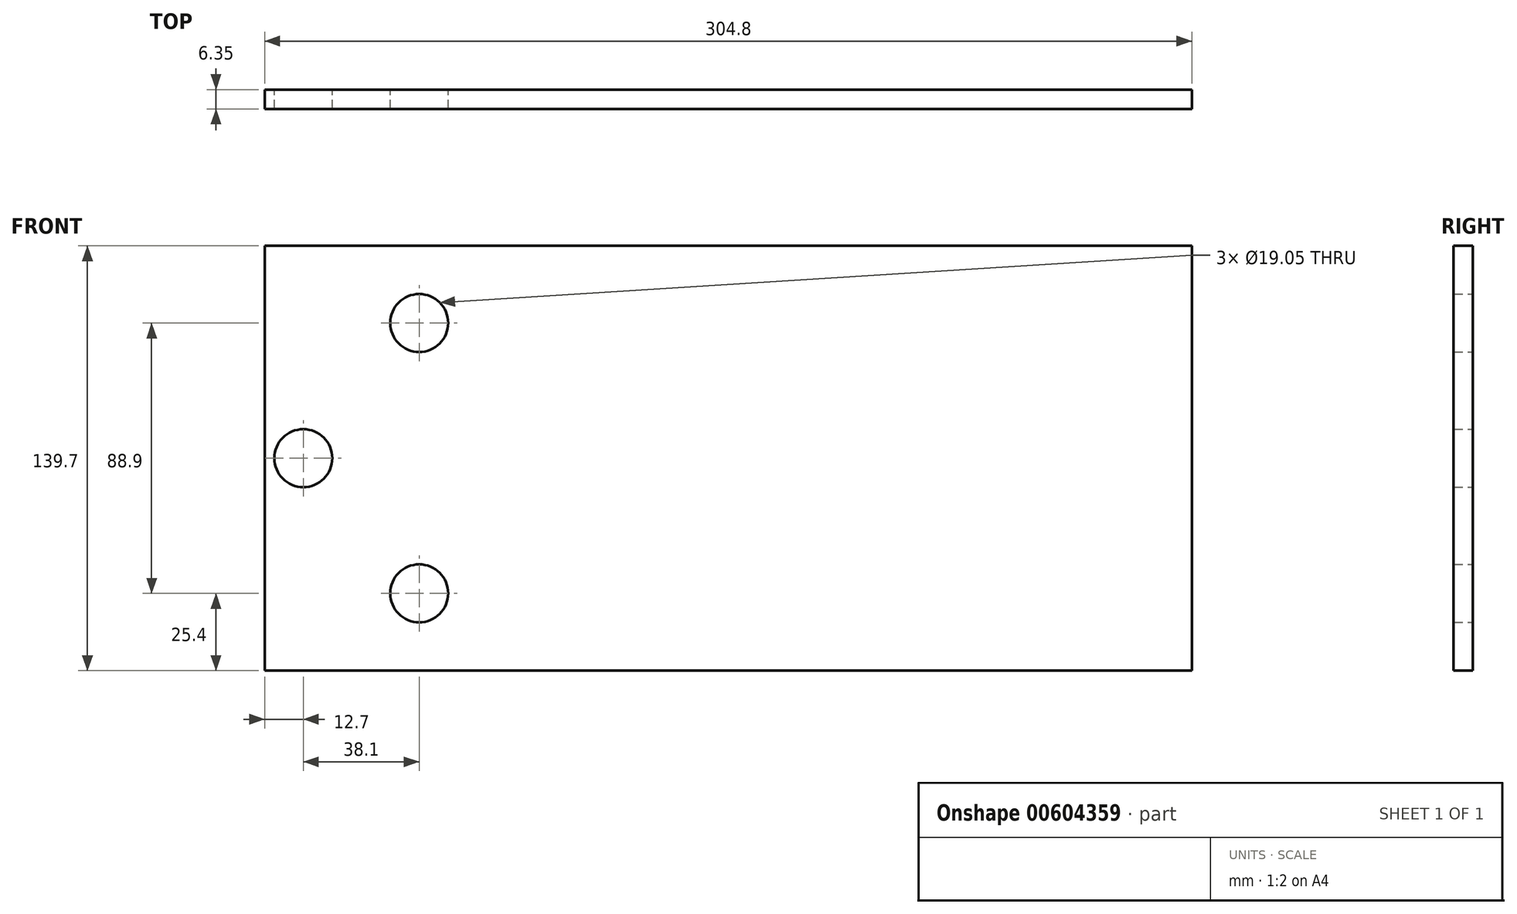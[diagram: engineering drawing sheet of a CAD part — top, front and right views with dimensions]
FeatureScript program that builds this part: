
annotation { "Feature Type Name" : "Feature", "Feature Type Description" : "" }
export const myFeature = defineFeature(function(context is Context, id is Id, definition is map)
    precondition{}
    {
        {
            var Q0;
            Q0=qCreatedBy(makeId("Front.planeOp"),FACE);
            var sketch = newSketch(context, id + "F0", { "sketchPlane" : qUnion([Q0])});
            skLineSegment(sketch, "E0.bottom", {"start": v(-152.4, 69.85) * mm, "end": v(152.4, 69.85) * mm});
            skLineSegment(sketch, "E0.top", {"start": v(-152.4, -69.85) * mm, "end": v(152.4, -69.85) * mm});
            skLineSegment(sketch, "E0.left", {"start": v(-152.4, 69.85) * mm, "end": v(-152.4, -69.85) * mm});
            skLineSegment(sketch, "E0.right", {"start": v(152.4, 69.85) * mm, "end": v(152.4, -69.85) * mm});
            skPoint(sketch, "E0.middle", {"position": v(0, 0) * mm});
            skSolve(sketch);
        }
        {
            var Q0;
            Q0=makeQuery(id+"F0.imprint","IMPRINT",FACE,{"disambiguationData":[TD([[makeQuery(id+"F0.imprint","IMPRINT",EDGE,{"derivedFrom":sQuery(id+"F0.wireOp",EDGE,"E0.bottom")}),-1.0]])]});
            extrude(context, id + "F1", {"entities" : qUnion([Q0]), "depth" : 6.35 * mm, "offsetDistance" : 25.4 * mm});
        }
        {
            var Q0;
            Q0=qCreatedBy(makeId("Front.planeOp"),FACE);
            var sketch = newSketch(context, id + "F2", { "sketchPlane" : qUnion([Q0])});
            skCircle(sketch, "E1", {"center": v(-139.7, 0) * mm, "radius": 9.53 * mm});
            skCircle(sketch, "E2", {"center": v(-101.6, 44.45) * mm, "radius": 9.53 * mm});
            skCircle(sketch, "E3", {"center": v(-101.6, -44.45) * mm, "radius": 9.53 * mm});
            skSolve(sketch);
        }
        {
            var Q0;
            Q0=sQuery(id+"F2.wireOp",VERTEX,"E2.center");
            var Q1;
            Q1=sQuery(id+"F2.wireOp",VERTEX,"E1.center");
            var Q2;
            Q2=sQuery(id+"F2.wireOp",VERTEX,"E3.center");
            var Q3;
            Q3=makeQuery(id+"F1.opExtrude","SWEPT_BODY",BODY,{"disambiguationData":[OSD([sQuery(id+"F0.wireOp",EDGE,"E0.bottom"),sQuery(id+"F0.wireOp",EDGE,"E0.top"),sQuery(id+"F0.wireOp",EDGE,"E0.left"),sQuery(id+"F0.wireOp",EDGE,"E0.right")])]});
            hole(context, id + "F3", {"style" : HoleStyle.SIMPLE, "endStyle" : HoleEndStyle.THROUGH, "oppositeDirection" : true, "holeDiameter" : 19.05 * mm, "majorDiameter" : 6.35 * mm, "isTappedThrough" : true, "tappedDepth" : 12.7 * mm, "tapClearance" : 3, "locations" : qUnion([Q0, Q1, Q2]), "scope" : qUnion([Q3])});
        }
    });
